FCSTD DOCUMENT  (FreeCAD 1.0R39319 (Git))
Label: ComplexNesting
License: All rights reserved
LicenseURL: https://en.wikipedia.org/wiki/All_rights_reserved
objects: Part::Part2DObjectPython×7, App::DocumentObjectGroupPython×3, App::DocumentObjectGroup×1
note: 7 computed .brp shape members not serialized (recipe doc carries the construction recipe); baked Part::Feature solids carry a one-line shape summary decoded from their .brp

FEATURE [Part::Part2DObjectPython] Circle001  label="Left"  # Draft 2D object (typed FeaturePython)
  Area = 1256.64
  FirstAngle = 0
  LastAngle = 0
  MakeFace = true
  Placement = pos=(-20,0,0) rot=(0,0,1;0rad)
  Radius = 20
FEATURE [Part::Part2DObjectPython] Circle003  label="Right"  # Draft 2D object (typed FeaturePython)
  Area = 201.062
  FirstAngle = 0
  LastAngle = 0
  MakeFace = true
  Placement = pos=(20,0,0) rot=(0,0,1;0rad)
  Radius = 8
FEATURE [App::DocumentObjectGroupPython] MaterialGroup  label="Materials"  # scripted group (container) (typed FeaturePython)
FEATURE [Part::Part2DObjectPython] Circle004  label="SubLeftA"  # Draft 2D object (typed FeaturePython)
  Area = 201.062
  FirstAngle = 0
  LastAngle = 0
  MakeFace = true
  Placement = pos=(-29,0,0) rot=(0,0,1;0rad)
  Radius = 8
FEATURE [Part::Part2DObjectPython] Circle005  label="SubLeftB"  # Draft 2D object (typed FeaturePython)
  Area = 201.062
  FirstAngle = 0
  LastAngle = 0
  MakeFace = true
  Placement = pos=(-11,0,0) rot=(0,0,1;0rad)
  Radius = 8
FEATURE [Part::Part2DObjectPython] Circle006  label="SubLeftA1"  # Draft 2D object (typed FeaturePython)
  Area = 12.5664
  FirstAngle = 0
  LastAngle = 0
  MakeFace = true
  Placement = pos=(-33,0,0) rot=(0,0,1;0rad)
  Radius = 2
FEATURE [Part::Part2DObjectPython] Circle007  label="SubLeftA2"  # Draft 2D object (typed FeaturePython)
  Area = 50.2655
  FirstAngle = 0
  LastAngle = 0
  MakeFace = true
  Placement = pos=(-26,0,0) rot=(0,0,1;0rad)
  Radius = 4
FEATURE [Part::Part2DObjectPython] Circle008  label="SubRightA"  # Draft 2D object (typed FeaturePython)
  Area = 12.5664
  FirstAngle = 0
  LastAngle = 0
  MakeFace = true
  Placement = pos=(20,0,0) rot=(0,0,1;0rad)
  Radius = 2
FEATURE [App::DocumentObjectGroup] Group  label="Conductors"
  Group = -> [Circle003,Circle001,Circle004,Circle005,Circle006,Circle007,Circle008]
FEATURE [App::DocumentObjectGroupPython] CaseStudy  label="Model"  # scripted group (container) (typed FeaturePython)
  Group = -> [Group]
FEATURE [App::DocumentObjectGroupPython] CrossSection  label="Cross-Section"  # scripted group (container) (typed FeaturePython)
  Group = -> [MaterialGroup,CaseStudy]
